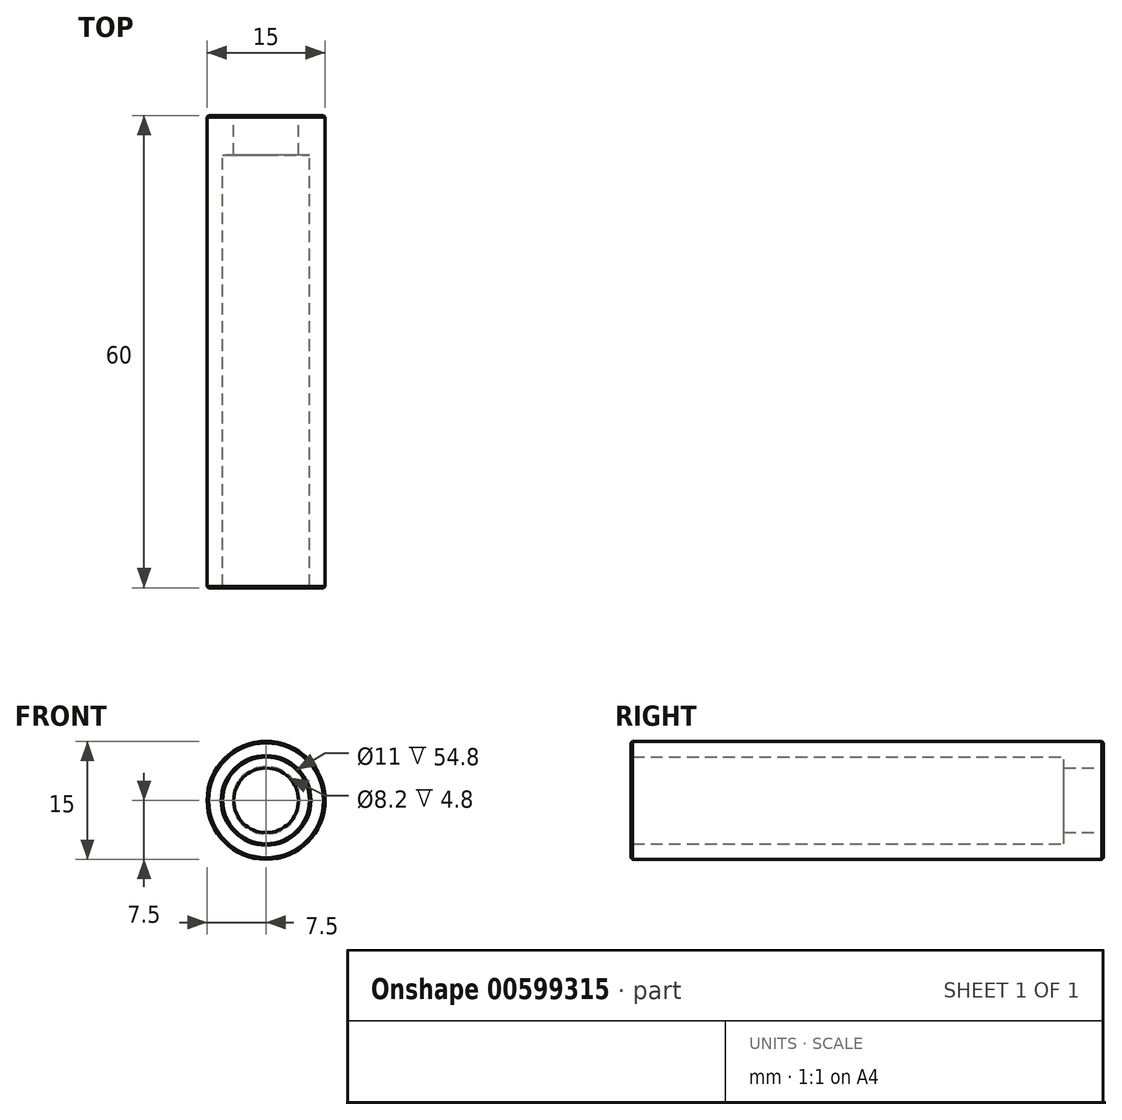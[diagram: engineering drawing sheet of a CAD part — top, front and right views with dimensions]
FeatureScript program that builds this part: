
annotation { "Feature Type Name" : "Feature", "Feature Type Description" : "" }
export const myFeature = defineFeature(function(context is Context, id is Id, definition is map)
    precondition{}
    {
        {
            var Q0;
            Q0=qCreatedBy(makeId("Front.planeOp"),FACE);
            var sketch = newSketch(context, id + "F0", { "sketchPlane" : qUnion([Q0])});
            skCircle(sketch, "E0", {"center": v(0, 0) * mm, "radius": 7.5 * mm});
            skCircle(sketch, "E1", {"center": v(0, 0) * mm, "radius": 4.1 * mm});
            skCircle(sketch, "E2", {"center": v(0, 0) * mm, "radius": 5.5 * mm});
            skSolve(sketch);
        }
        {
            var Q0;
            Q0=makeQuery(id+"F0.imprint","IMPRINT",FACE,{"disambiguationData":[TD([[makeQuery(id+"F0.imprint","IMPRINT",EDGE,{"derivedFrom":sQuery(id+"F0.wireOp",EDGE,"E0")}),1.0]])]});
            extrude(context, id + "F1", {"entities" : qUnion([Q0]), "depth" : 60 * mm, "offsetDistance" : 25 * mm});
        }
        {
            var Q0;
            Q0=makeQuery(id+"F0.imprint","IMPRINT",FACE,{"disambiguationData":[TD([[makeQuery(id+"F0.imprint","IMPRINT",EDGE,{"derivedFrom":sQuery(id+"F0.wireOp",EDGE,"E1")}),-1.0]])]});
            extrude(context, id + "F2", {"entities" : qUnion([Q0]), "operationType" : NewBodyOperationType.ADD, "depth" : 5 * mm, "offsetDistance" : 25 * mm});
        }
        {
            var Q0;
            {var subQ0=sQuery(id+"F0.wireOp",EDGE,"E2");Q0=makeQuery(id+"F2.boolean.opBoolean","MERGE",FACE,{"derivedFrom":[makeQuery(id+"F1.opExtrude","CAP_FACE",FACE,{"disambiguationData":[OSD([sQuery(id+"F0.wireOp",EDGE,"E0"),subQ0])],"isStart":true}),makeQuery(id+"F2.opExtrude","CAP_FACE",FACE,{"disambiguationData":[OSD([sQuery(id+"F0.wireOp",EDGE,"E1"),subQ0])],"isStart":true})]});}
            var Q1;
            Q1=makeQuery(id+"F1.opExtrude","CAP_FACE",FACE,{"disambiguationData":[OSD([sQuery(id+"F0.wireOp",EDGE,"E0"),sQuery(id+"F0.wireOp",EDGE,"E2")])],"isStart":false});
            chamfer(context, id + "F3", {"entities" : qUnion([Q0, Q1]), "width" : .2 * mm, "tangentPropagation" : true});
        }
    });
